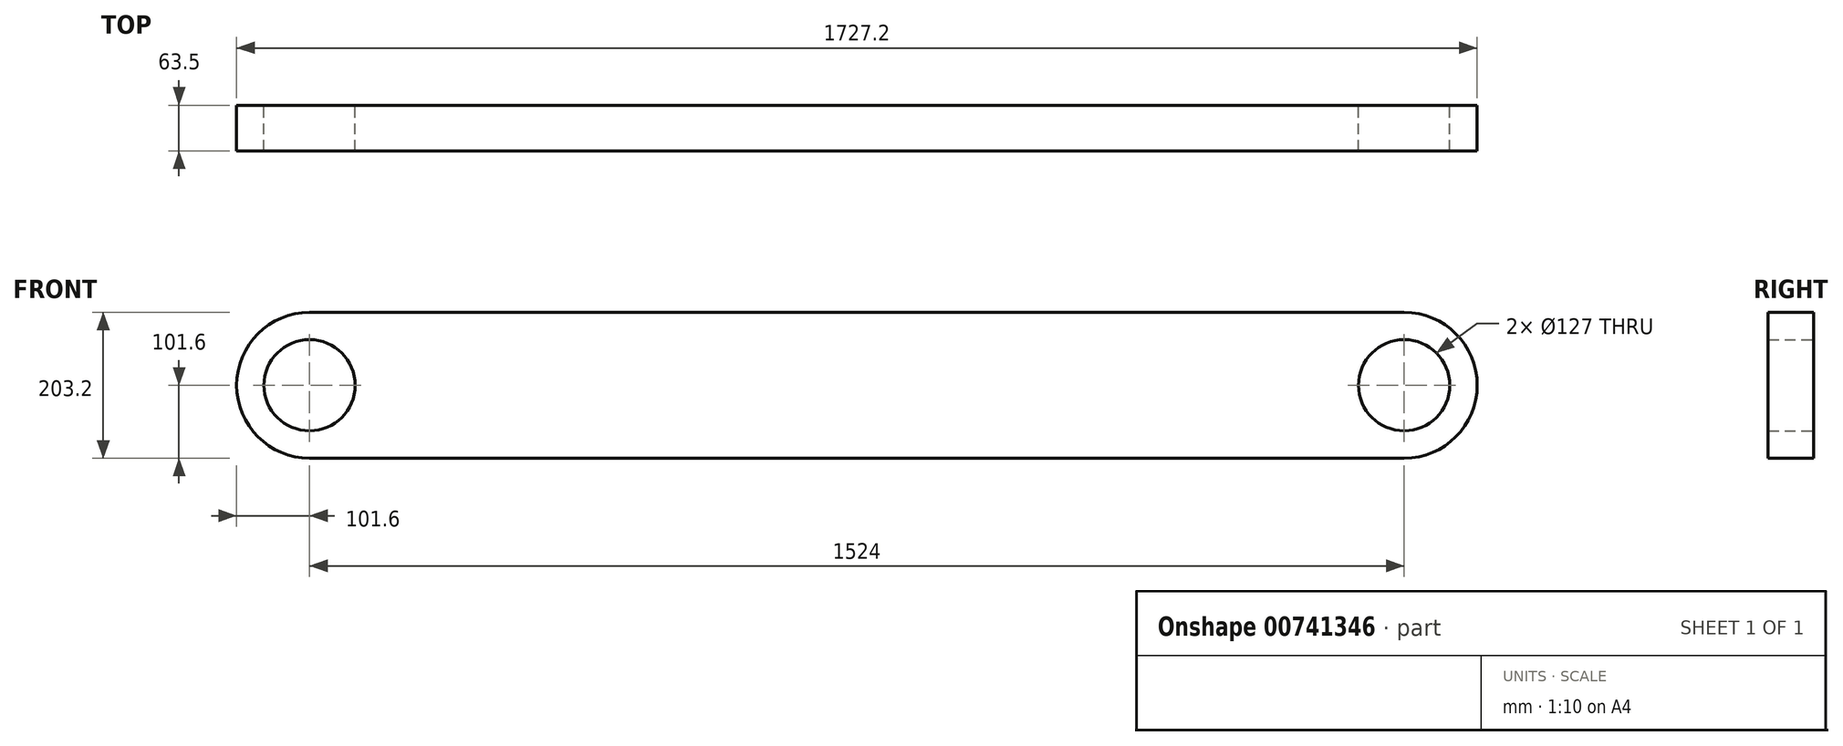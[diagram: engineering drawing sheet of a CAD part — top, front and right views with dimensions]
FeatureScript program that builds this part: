
annotation { "Feature Type Name" : "Feature", "Feature Type Description" : "" }
export const myFeature = defineFeature(function(context is Context, id is Id, definition is map)
    precondition{}
    {
        {
            var Q0;
            Q0=qCreatedBy(makeId("Front.planeOp"),FACE);
            var sketch = newSketch(context, id + "F0", { "sketchPlane" : qUnion([Q0])});
            skPoint(sketch, "E0.middle", {"position": v(0, 0) * mm});
            skArc(sketch, "E1", {"start": v(762, 101.6) * mm, "mid": v(863.6, 0) * mm, "end": v(762, -101.6) * mm});
            skArc(sketch, "E2", {"start": v(-762, 101.6) * mm, "mid": v(-863.6, 0) * mm, "end": v(-762, -101.6) * mm});
            skCircle(sketch, "E3", {"center": v(-762, 0) * mm, "radius": 63.5 * mm});
            skCircle(sketch, "E4", {"center": v(762, 0) * mm, "radius": 63.5 * mm});
            skLineSegment(sketch, "E5", {"start": v(-762, -101.6) * mm, "end": v(762, -101.6) * mm});
            skLineSegment(sketch, "E6", {"start": v(-762, 101.6) * mm, "end": v(762, 101.6) * mm});
            skSolve(sketch);
        }
        {
            var Q0;
            Q0 = qSketchRegion(id + "F0", true);
            extrude(context, id + "F1", {"entities" : qUnion([Q0]), "endBound" : BoundingType.SYMMETRIC, "depth" : 63.5 * mm, "offsetDistance" : 25.4 * mm});
        }
    });
